AUTODESK INVENTOR PART (.ipt)
format: ipt  version: 2014 (Build 180170000, 170)  size: 95,232 bytes
history: native  units: mm
features: extrude x2, sketch x2, reference x1
ambient origin geometry x8: Origin, YZ Plane, XZ Plane, XY Plane, X Axis, Y Axis, Z Axis, Center Point
bodies: Solid1 (feature_tree)
feature tree (5):
  extrude  "Extrusion1"  Depth=50.0mm
  extrude  "Extrusion2"  Depth=10.0mm
  sketch  "Sketch1"  dims[d0=2.4mm d1=0.0mm d2=50.0mm]
  reference  "Reference1"
  sketch  "Sketch2"  dims[d3=60.0mm d4=10.0mm d5=2.5mm d6=6.0mm d7=2.5mm d8=6.0mm d9=2.5mm d10=6.0mm d11=2.5mm d12=6.0mm d13=4.0mm d14=0.0mm]
